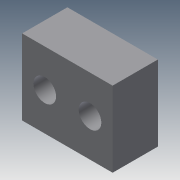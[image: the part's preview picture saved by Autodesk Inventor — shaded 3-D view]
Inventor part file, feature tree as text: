
AUTODESK INVENTOR PART (.ipt)
format: ipt  version: 2015 (Build 190159000, 159)  size: 101,888 bytes
history: native  units: mm
features: extrude x4, sketch x4
ambient origin geometry x8: Origin, YZ Plane, XZ Plane, XY Plane, X Axis, Y Axis, Z Axis, Center Point
bodies: Solid1 (feature_tree)
feature tree (8):
  extrude  "Extrusion1"  Depth=10.0mm
  extrude  "Extrusion2"  Depth=3.0mm
  extrude  "Extrusion3"  Depth=3.0mm
  extrude  "Extrusion4"  Depth=6.0mm TaperAngle=0.0deg
  sketch  "Sketch1"  dims[d0=12.0mm d1=10.0mm]
  sketch  "Sketch2"  dims[d2=6.0mm d3=0.0mm d4=3.0mm]
  sketch  "Sketch3"  dims[d5=3.0mm d6=3.0mm]
  sketch  "Sketch4"  dims[d7=3.0mm d8=6.0mm d9=0.0mm d10=6.0mm d11=0.0mm d12=3.0mm d13=6.0mm d14=3.0mm d15=3.0mm d16=6.0mm d17=0.0mm]
